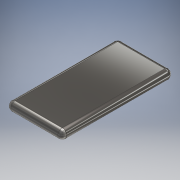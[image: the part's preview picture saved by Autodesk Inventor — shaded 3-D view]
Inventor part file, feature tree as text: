
AUTODESK INVENTOR PART (.ipt)
format: ipt  version: 2018 (Build 220112000, 112)  size: 119,296 bytes
history: native  units: mm
features: extrude x1, fillet x1, sketch x1
ambient origin geometry x8: Origin, YZ Plane, XZ Plane, XY Plane, X Axis, Y Axis, Z Axis, Center Point
bodies: Solid1 (feature_tree)
feature tree (3):
  extrude  "Extrusion1"  Depth=6.0mm
  fillet  "Fillet1"  Radius=12.0mm
  sketch  "Sketch1"  dims[d0=73.0mm d1=145.0mm d2=12.0mm d3=0.0mm d4=6.0mm]
